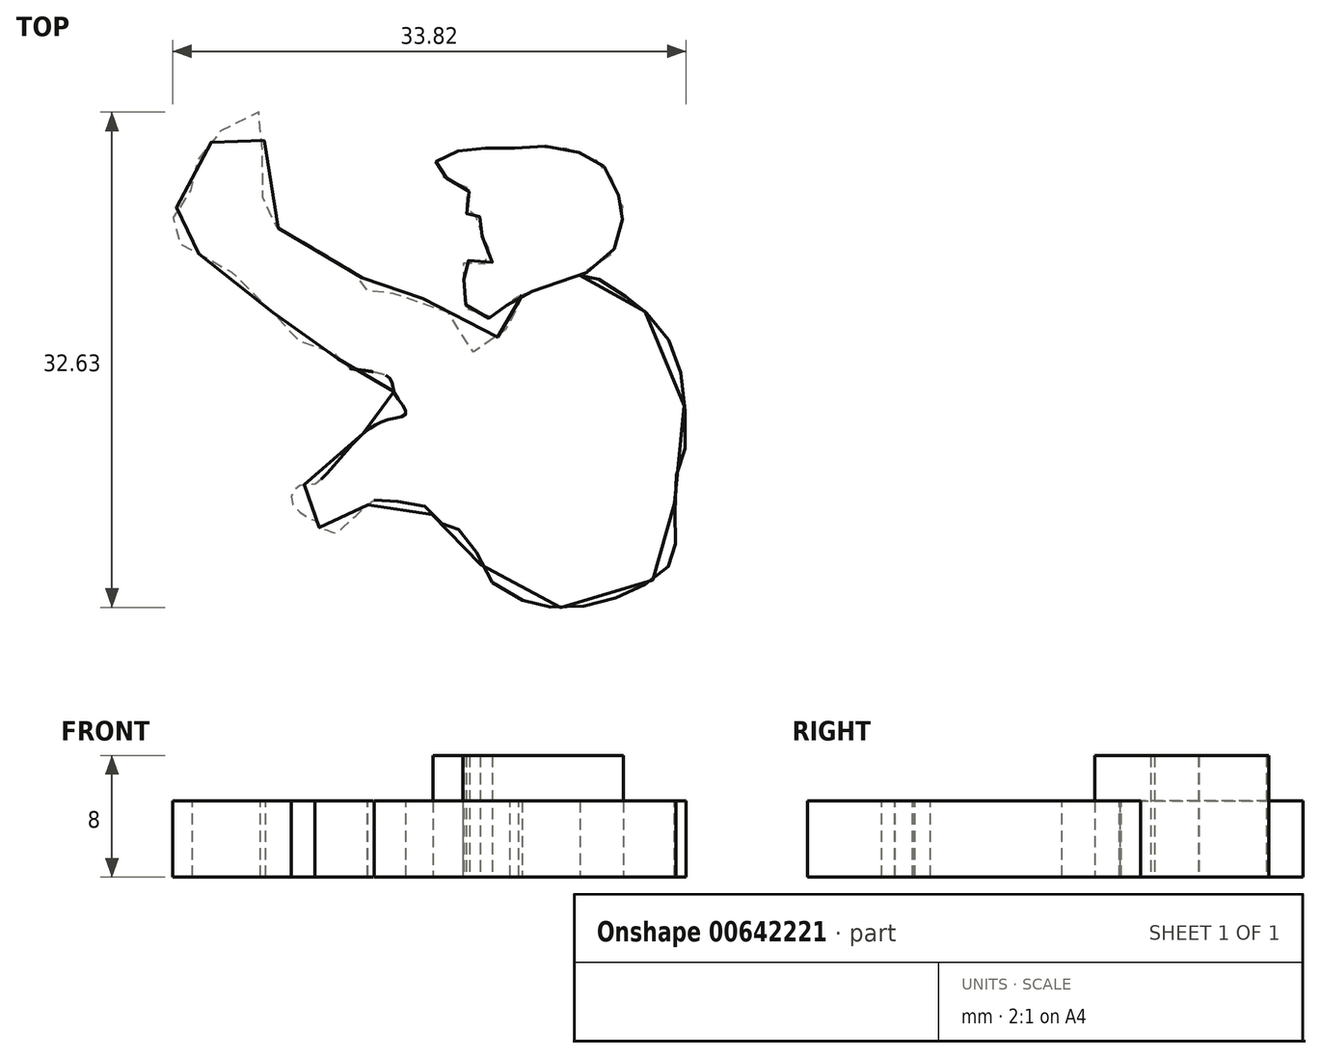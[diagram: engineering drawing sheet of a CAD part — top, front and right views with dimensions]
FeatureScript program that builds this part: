
annotation { "Feature Type Name" : "Feature", "Feature Type Description" : "" }
export const myFeature = defineFeature(function(context is Context, id is Id, definition is map)
    precondition{}
    {
        {
            var Q0;
            Q0=qCreatedBy(makeId("Top.planeOp"),FACE);
            var sketch = newSketch(context, id + "F0", { "sketchPlane" : qUnion([Q0])});
            skFitSpline(sketch, "E0", {"points": [v(-7.36, 16.88) * mm, v(-6.3, 17.84) * mm, v(-5.1, 18.87) * mm, v(-5.1, 18.76) * mm, v(-2.44, 18.76) * mm, v(-1.58, 18.22) * mm, v(-0.49, 17.23) * mm, v(0, 17.09) * mm, v(1.19, 16.3) * mm, v(2.35, 13.8) * mm, v(4.8, 12.2) * mm, v(6.76, 11.8) * mm, v(9.5, 12.02) * mm, v(11.82, 12.86) * mm, v(13.95, 14.1) * mm, v(14.65, 15.31) * mm, v(14.75, 17.23) * mm, v(14.78, 20.48) * mm, v(15.37, 22.25) * mm, v(15.25, 25.82) * mm, v(14.64, 28.79) * mm, v(12.8, 31.2) * mm, v(11.5, 32.23) * mm, v(9.52, 33.52) * mm, v(8.83, 33.72) * mm, v(6.22, 33.03) * mm, v(4.65, 32.36) * mm, v(3.85, 31.73) * mm, v(4.24, 31.51) * mm, v(4.4, 30.94) * mm, v(3.42, 29.96) * mm, v(1.53, 28.55) * mm, v(0, 30.96) * mm, v(-4.2, 32.45) * mm, v(-5.51, 32.38) * mm, v(-5.51, 32.9) * mm, v(-5.67, 33.32) * mm, v(-7.25, 34.39) * mm, v(-9.64, 35.77) * mm, v(-11.95, 37.23) * mm, v(-12.4, 38.6) * mm, v(-12.54, 41.35) * mm, v(-12.44, 44.32) * mm, v(-14.62, 43.65) * mm, v(-15.95, 42.28) * mm, v(-17.02, 40.6) * mm, v(-17.15, 39.35) * mm, v(-18.12, 38.12) * mm, v(-18.37, 36.8) * mm, v(-18.05, 35.83) * mm, v(-17.12, 35.5) * mm, v(-16.63, 35.06) * mm, v(-15.83, 34.9) * mm, v(-13.05, 32.41) * mm, v(-11.05, 30.48) * mm, v(-9.08, 28.7) * mm, v(-7.57, 28.45) * mm, v(-7.4, 27.87) * mm, v(-5.96, 27.41) * mm, v(-4.08, 26.9) * mm, v(-3.76, 25.93) * mm, v(-3, 24.57) * mm, v(-4.24, 24.13) * mm, v(-5.66, 23.37) * mm, v(-6.85, 22.18) * mm, v(-8.92, 19.95) * mm, v(-9.42, 19.88) * mm, v(-10.19, 19.68) * mm, v(-10.46, 18.53) * mm, v(-9, 17.53) * mm, v(-9, 17.57) * mm, v(-8.72, 17.05) * mm, v(-8.18, 16.88) * mm, v(-7.73, 16.68) * mm, v(-7.36, 16.88) * mm]});
            skSolve(sketch);
        }
        {
            var Q0;
            Q0=qCreatedBy(makeId("Top.planeOp"),FACE);
            var sketch = newSketch(context, id + "F1", { "sketchPlane" : qUnion([Q0])});
            skFitSpline(sketch, "E1", {"points": [v(3.64, 31.68) * mm, v(3.09, 31.33) * mm, v(2, 30.72) * mm, v(0.78, 32.1) * mm, v(0.81, 33.28) * mm, v(0.81, 34.49) * mm, v(1.53, 34.6) * mm, v(2.65, 34.47) * mm, v(2.17, 35.93) * mm, v(1.9, 36.66) * mm, v(1.83, 37.53) * mm, v(1.57, 37.56) * mm, v(1.06, 37.61) * mm, v(1, 38.06) * mm, v(1.14, 39.2) * mm, v(0.13, 39.94) * mm, v(-1.2, 40.52) * mm, v(-0.63, 41.53) * mm, v(0.43, 41.85) * mm, v(1.94, 42.02) * mm, v(3.53, 42.02) * mm, v(5.3, 42.12) * mm, v(7.35, 42.06) * mm, v(9.52, 41.23) * mm, v(10.28, 40.5) * mm, v(11.2, 38.35) * mm, v(11.28, 37.46) * mm, v(10.83, 35.72) * mm, v(9.47, 34.12) * mm, v(4.33, 32.2) * mm, v(3.64, 31.68) * mm]});
            skSolve(sketch);
        }
        {
            var Q0;
            Q0 = qSketchRegion(id + "F1", true);
            extrude(context, id + "F2", {"entities" : qUnion([Q0]), "depth" : 8 * mm, "offsetDistance" : 25.4 * mm});
        }
        {
            var Q0;
            Q0 = qSketchRegion(id + "F0", true);
            extrude(context, id + "F3", {"entities" : qUnion([Q0]), "operationType" : NewBodyOperationType.ADD, "depth" : 5 * mm, "offsetDistance" : 25.4 * mm});
        }
    });
